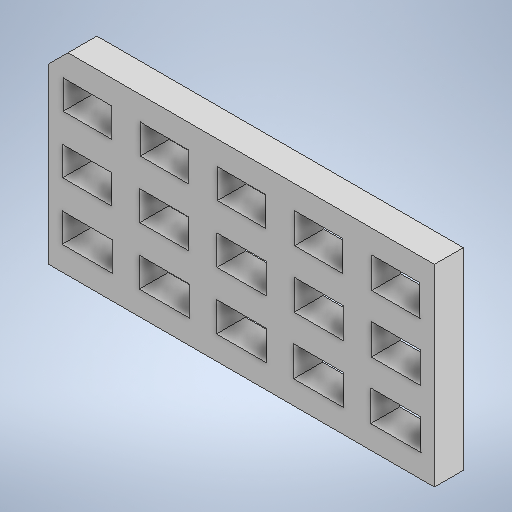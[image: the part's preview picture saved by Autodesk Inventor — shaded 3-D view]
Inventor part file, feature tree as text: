
AUTODESK INVENTOR PART (.ipt)
format: ipt  version: 2025.3 (Build 293356000, 356)  size: 302,592 bytes
history: native  units: mm
features: extrude x2, sketch x2, other x1, chamfer x1
ambient origin geometry x8: Origin, YZ Plane, XZ Plane, XY Plane, X Axis, Y Axis, Z Axis, Center Point
bodies: Body1 (feature_tree)
feature tree (6):
  other  "ソリッド1"
  extrude  "ベース"  Depth=40.0mm
  extrude  "押し出し2"  Depth=20.0mm
  chamfer  "面取り1"  Distance=3.0mm
  sketch  "スケッチ1"
  sketch  "スケッチ2"
